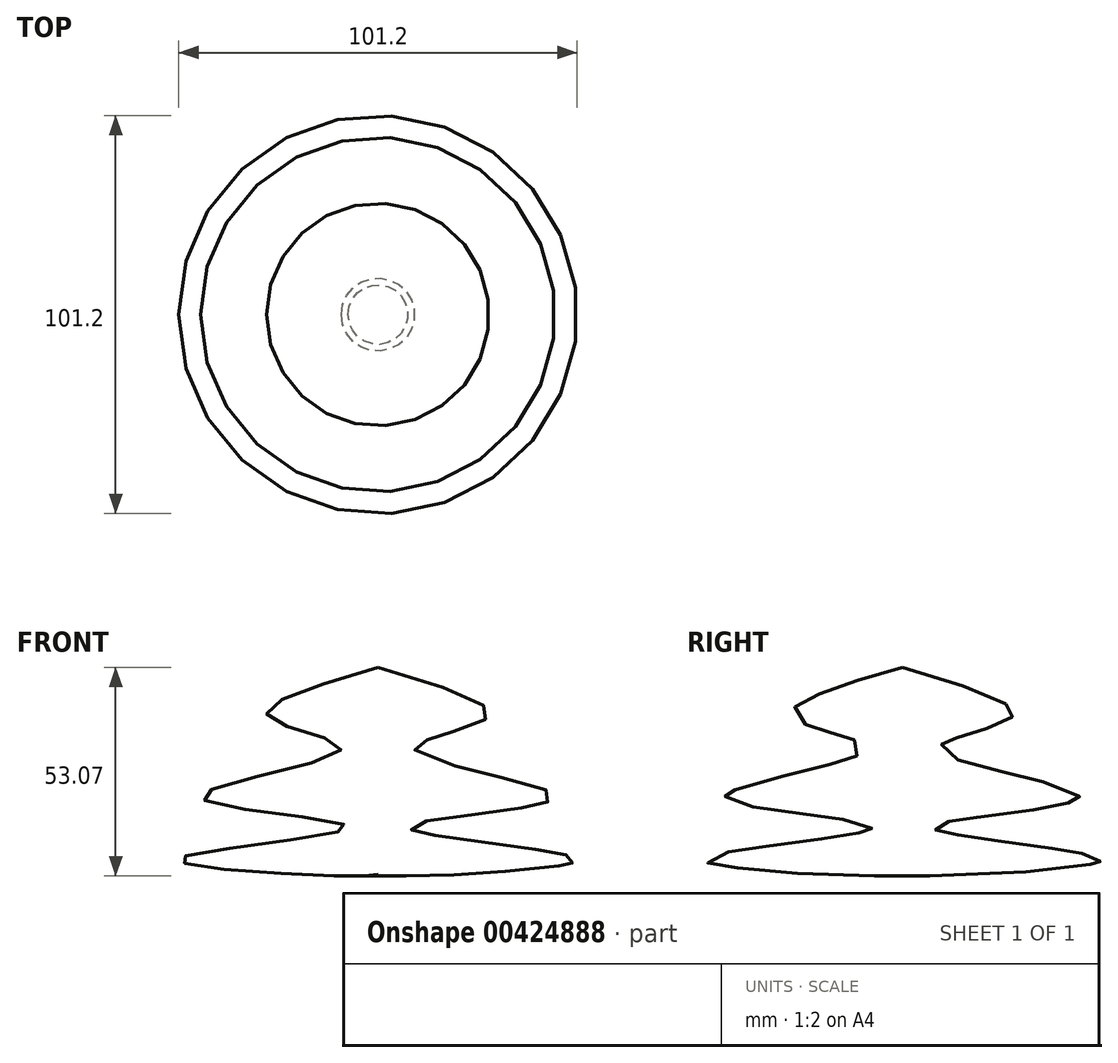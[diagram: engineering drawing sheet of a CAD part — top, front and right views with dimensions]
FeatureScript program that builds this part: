
annotation { "Feature Type Name" : "Feature", "Feature Type Description" : "" }
export const myFeature = defineFeature(function(context is Context, id is Id, definition is map)
    precondition{}
    {
        {
            var Q0;
            Q0=qCreatedBy(makeId("Front.planeOp"),FACE);
            var sketch = newSketch(context, id + "F0", { "sketchPlane" : qUnion([Q0])});
            skFitSpline(sketch, "E0", {"points": [v(0, 59.74) * mm, v(-27.64, 46.81) * mm, v(-9.36, 38.79) * mm, v(-45.03, 26.75) * mm, v(-7.58, 19.17) * mm, v(-50.38, 11.15) * mm, v(-9.36, 6.69) * mm, v(0, 7.13) * mm], "startDerivative": vector(-330.08, -96.88) * mm, "endDerivative": vector(63.16, 10.26) * mm});
            skLineSegment(sketch, "E1", {"start": v(0, 59.74) * mm, "end": v(0, 7.13) * mm});
            skSolve(sketch);
        }
        {
            var Q0;
            Q0=makeQuery(id+"F0.imprint","IMPRINT",FACE,{"disambiguationData":[TD([[makeQuery(id+"F0.imprint","IMPRINT",EDGE,{"derivedFrom":sQuery(id+"F0.wireOp",EDGE,"E0")}),1.0]])]});
            var Q1;
            Q1=sQuery(id+"F0.wireOp",EDGE,"E1");
            revolve(context, id + "F1", {"entities" : qUnion([Q0]), "axis" : qUnion([Q1]), "revolveType" : RevolveType.FULL});
        }
    });
